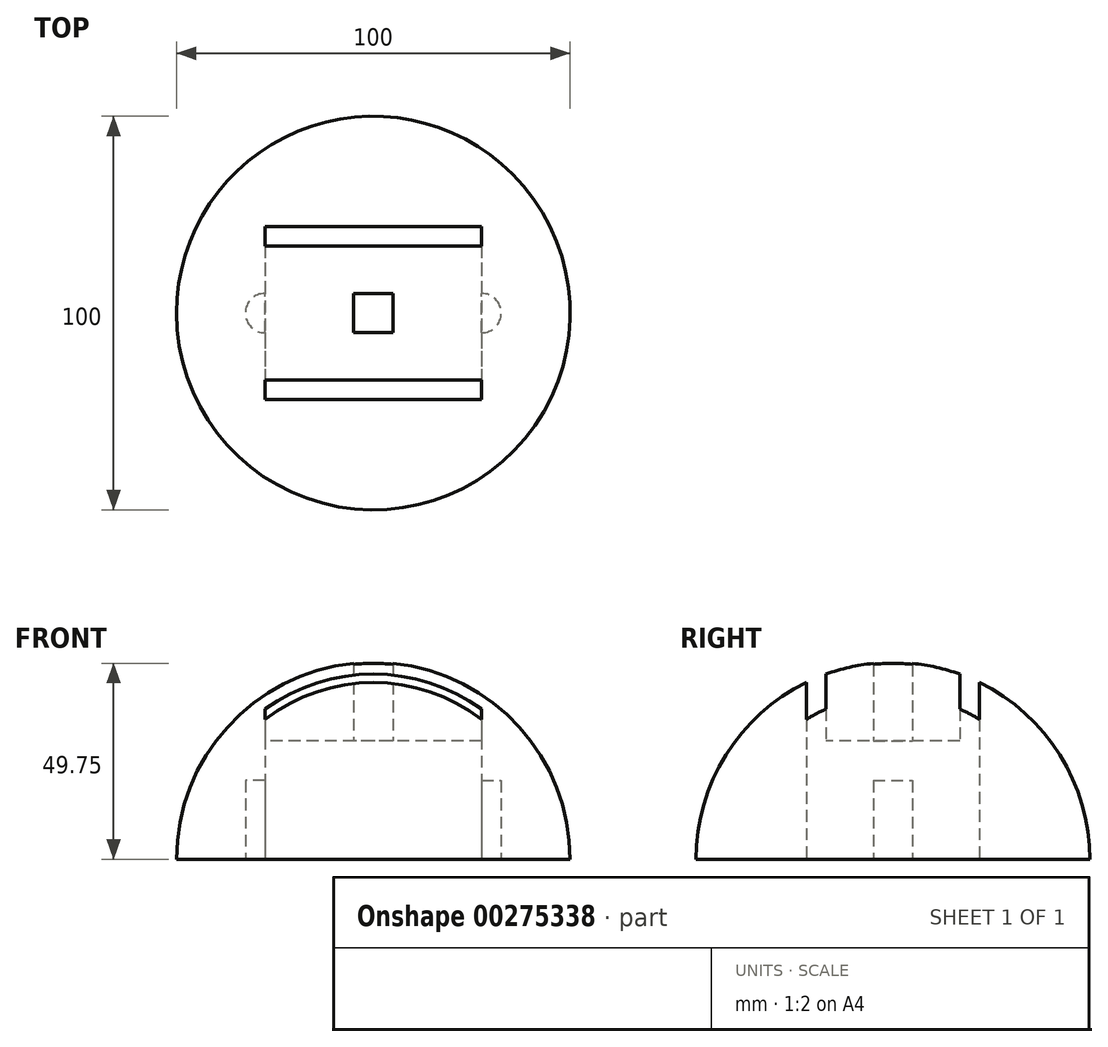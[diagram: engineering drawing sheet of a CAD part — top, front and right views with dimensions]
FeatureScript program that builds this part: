
annotation { "Feature Type Name" : "Feature", "Feature Type Description" : "" }
export const myFeature = defineFeature(function(context is Context, id is Id, definition is map)
    precondition{}
    {
        {
            var Q0;
            Q0=qCreatedBy(makeId("Top.planeOp"),FACE);
            var sketch = newSketch(context, id + "F0", { "sketchPlane" : qUnion([Q0])});
            skLineSegment(sketch, "E0.bottom", {"start": v(-27.5, 22) * mm, "end": v(27.5, 22) * mm});
            skLineSegment(sketch, "E0.top", {"start": v(-27.5, -22) * mm, "end": v(27.5, -22) * mm});
            skLineSegment(sketch, "E0.left", {"start": v(-27.5, 22) * mm, "end": v(-27.5, -22) * mm});
            skLineSegment(sketch, "E0.right", {"start": v(27.5, 22) * mm, "end": v(27.5, -22) * mm});
            skPoint(sketch, "E0.middle", {"position": v(0, 0) * mm});
            skCircle(sketch, "E1", {"center": v(0, 0) * mm, "radius": 50 * mm});
            skLineSegment(sketch, "E2", {"start": v(27.5, -22) * mm, "end": v(27.5, -17) * mm});
            skLineSegment(sketch, "E3.bottom", {"start": v(27.5, -17) * mm, "end": v(-27.5, -17) * mm});
            skLineSegment(sketch, "E3.top", {"start": v(27.5, 17) * mm, "end": v(-27.5, 17) * mm});
            skLineSegment(sketch, "E3.left", {"start": v(27.5, -17) * mm, "end": v(27.5, 17) * mm});
            skLineSegment(sketch, "E3.right", {"start": v(-27.5, -17) * mm, "end": v(-27.5, 17) * mm});
            skLineSegment(sketch, "E4.bottom", {"start": v(5, -5) * mm, "end": v(-5, -5) * mm});
            skLineSegment(sketch, "E4.top", {"start": v(5, 5) * mm, "end": v(-5, 5) * mm});
            skLineSegment(sketch, "E4.left", {"start": v(5, -5) * mm, "end": v(5, 5) * mm});
            skLineSegment(sketch, "E4.right", {"start": v(-5, -5) * mm, "end": v(-5, 5) * mm});
            skPoint(sketch, "E5.center.orphan", {"position": v(-50, 0) * mm});
            skPoint(sketch, "E6.center.orphan", {"position": v(50, 0) * mm});
            skArc(sketch, "E7", {"start": v(-27.5, 5) * mm, "mid": v(-32.5, 0) * mm, "end": v(-27.5, -5) * mm});
            skArc(sketch, "E8", {"start": v(27.5, -5) * mm, "mid": v(32.5, 0) * mm, "end": v(27.5, 5) * mm});
            skSolve(sketch);
        }
        {
            var Q0;
            Q0=qCreatedBy(makeId("Front.planeOp"),FACE);
            var sketch = newSketch(context, id + "F1", { "sketchPlane" : qUnion([Q0])});
            skLineSegment(sketch, "E9", {"start": v(0, 0) * mm, "end": v(0, 50) * mm});
            skArc(sketch, "E10", {"start": v(0, 50) * mm, "mid": v(-35.36, 35.36) * mm, "end": v(-50, 0) * mm});
            skLineSegment(sketch, "E11", {"start": v(0, 0) * mm, "end": v(-50, 0) * mm});
            skSolve(sketch);
        }
        {
            var Q0;
            Q0 = qSketchRegion(id + "F1", true);
            var Q1;
            Q1=sQuery(id+"F1.wireOp",EDGE,"E9");
            revolve(context, id + "F2", {"entities" : qUnion([Q0]), "axis" : qUnion([Q1]), "revolveType" : RevolveType.FULL});
        }
        {
            var Q0;
            {var subQ0=sQuery(id+"F0.wireOp",EDGE,"E0.top");Q0=makeQuery(id+"F0.imprint","IMPRINT",FACE,{"disambiguationData":[TD([[makeQuery(id+"F0.imprint","IMPRINT",EDGE,{"derivedFrom":subQ0}),1.0]])]});}
            var Q1;
            {var subQ0=sQuery(id+"F0.wireOp",EDGE,"E0.bottom");Q1=makeQuery(id+"F0.imprint","IMPRINT",FACE,{"disambiguationData":[TD([[makeQuery(id+"F0.imprint","IMPRINT",EDGE,{"derivedFrom":subQ0}),-1.0]])]});}
            var Q2;
            Q2=makeQuery(id+"F0.imprint","IMPRINT",FACE,{"disambiguationData":[TD([[makeQuery(id+"F0.imprint","IMPRINT",EDGE,{"derivedFrom":sQuery(id+"F0.wireOp",EDGE,"E4.bottom")}),-1.0]])]});
            extrude(context, id + "F3", {"entities" : qUnion([Q0, Q1, Q2]), "operationType" : NewBodyOperationType.REMOVE, "depth" : 100 * mm});
        }
        {
            var Q0;
            Q0=makeQuery(id+"F0.imprint","IMPRINT",FACE,{"disambiguationData":[TD([[makeQuery(id+"F0.imprint","IMPRINT",EDGE,{"derivedFrom":sQuery(id+"F0.wireOp",EDGE,"E3.bottom")}),-1.0]])]});
            extrude(context, id + "F4", {"entities" : qUnion([Q0]), "operationType" : NewBodyOperationType.REMOVE, "depth" : 30 * mm});
        }
        {
            var Q0;
            Q0=qCreatedBy(makeId("Top.planeOp"),FACE);
            var sketch = newSketch(context, id + "F5", { "sketchPlane" : qUnion([Q0])});
            skLineSegment(sketch, "E12.bottom", {"start": v(-27.5, -22) * mm, "end": v(27.5, -22) * mm});
            skLineSegment(sketch, "E12.top", {"start": v(-27.5, 22) * mm, "end": v(27.5, 22) * mm});
            skLineSegment(sketch, "E12.left", {"start": v(-27.5, -22) * mm, "end": v(-27.5, 22) * mm});
            skLineSegment(sketch, "E12.right", {"start": v(27.5, -22) * mm, "end": v(27.5, 22) * mm});
            skPoint(sketch, "E12.middle", {"position": v(0, 0) * mm});
            skArc(sketch, "E13", {"start": v(27.5, -5) * mm, "mid": v(32.5, 0) * mm, "end": v(27.5, 5) * mm});
            skArc(sketch, "E14", {"start": v(-27.5, 5) * mm, "mid": v(-32.5, 0) * mm, "end": v(-27.5, -5) * mm});
            skSolve(sketch);
        }
        {
            var Q0;
            {var subQ0=sQuery(id+"F5.wireOp",EDGE,"E14");Q0=makeQuery(id+"F5.imprint","IMPRINT",FACE,{"disambiguationData":[TD([[makeQuery(id+"F5.imprint","IMPRINT",EDGE,{"derivedFrom":subQ0}),1.0]])]});}
            var Q1;
            {var subQ0=sQuery(id+"F5.wireOp",EDGE,"E13");Q1=makeQuery(id+"F5.imprint","IMPRINT",FACE,{"disambiguationData":[TD([[makeQuery(id+"F5.imprint","IMPRINT",EDGE,{"derivedFrom":subQ0}),1.0]])]});}
            extrude(context, id + "F6", {"entities" : qUnion([Q0, Q1]), "operationType" : NewBodyOperationType.REMOVE, "depth" : 20 * mm});
        }
    });
